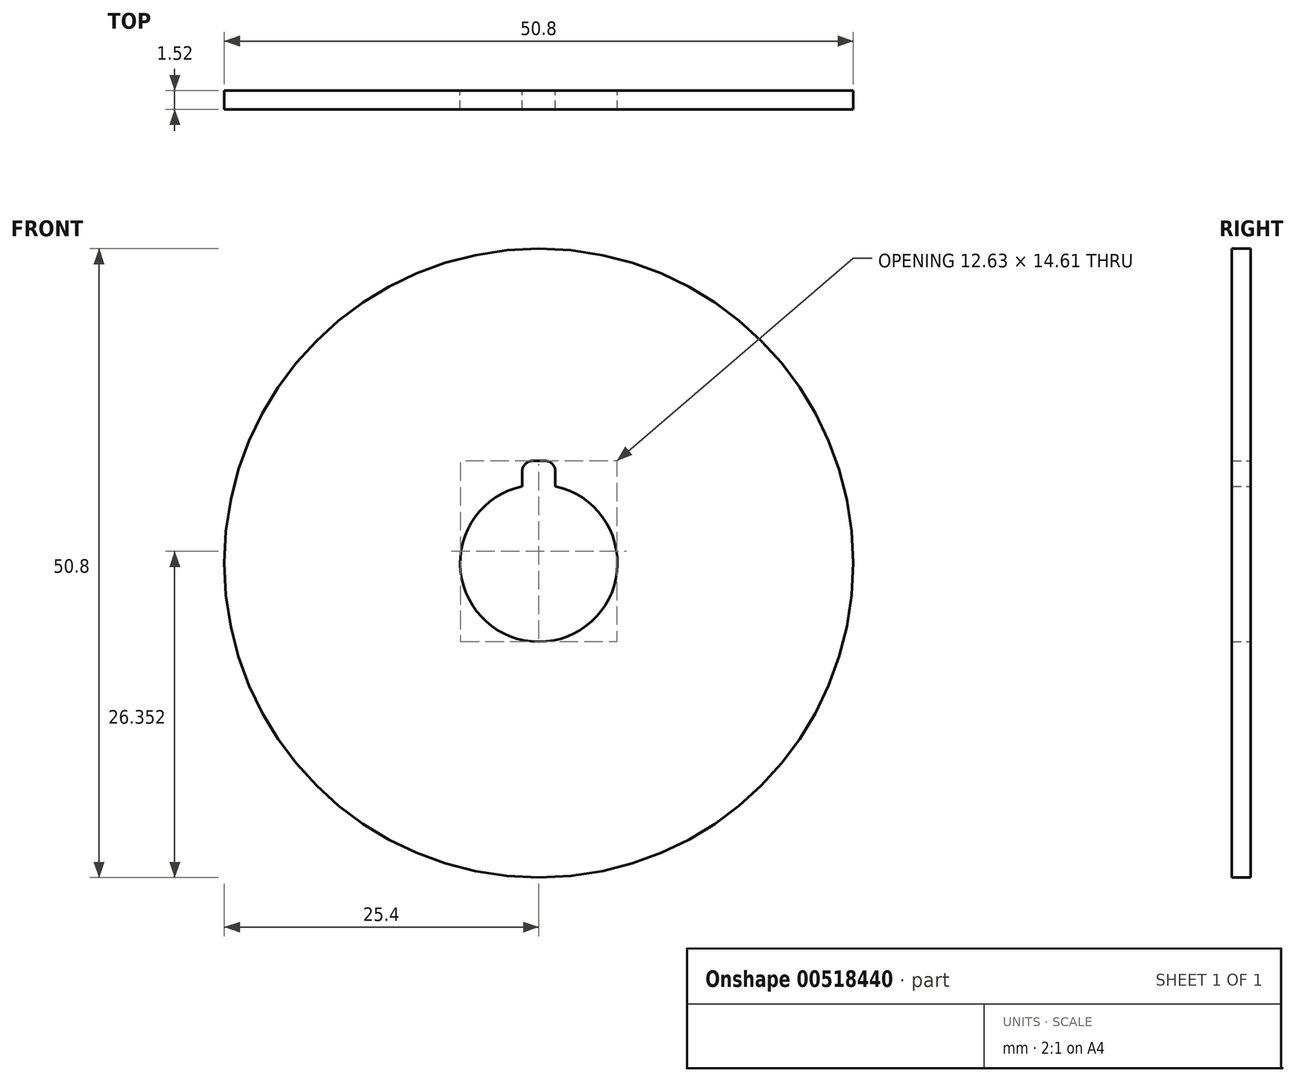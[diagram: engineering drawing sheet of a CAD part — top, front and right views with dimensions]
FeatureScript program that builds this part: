
annotation { "Feature Type Name" : "Feature", "Feature Type Description" : "" }
export const myFeature = defineFeature(function(context is Context, id is Id, definition is map)
    precondition{}
    {
        {
            var Q0;
            Q0=qCreatedBy(makeId("Front.planeOp"),FACE);
            var sketch = newSketch(context, id + "F0", { "sketchPlane" : qUnion([Q0])});
            skCircle(sketch, "E0", {"center": v(0, 0) * mm, "radius": 6.35 * mm});
            skCircle(sketch, "E1", {"center": v(0, 0) * mm, "radius": 25.4 * mm});
            skSolve(sketch);
        }
        {
            var Q0;
            Q0 = qSketchRegion(id + "F0", true);
            extrude(context, id + "F1", {"entities" : qUnion([Q0]), "depth" : 1.52 * mm, "offsetDistance" : 25.4 * mm});
        }
        {
            var Q0;
            Q0=qCreatedBy(makeId("Front.planeOp"),FACE);
            var sketch = newSketch(context, id + "F2", { "sketchPlane" : qUnion([Q0])});
            skLineSegment(sketch, "E2.bottom", {"start": v(-1.33, 8.25) * mm, "end": v(1.33, 8.25) * mm});
            skLineSegment(sketch, "E2.top", {"start": v(-1.33, 0) * mm, "end": v(1.33, 0) * mm});
            skLineSegment(sketch, "E2.left", {"start": v(-1.33, 8.25) * mm, "end": v(-1.33, 0) * mm});
            skLineSegment(sketch, "E2.right", {"start": v(1.33, 8.25) * mm, "end": v(1.33, 0) * mm});
            skPoint(sketch, "E3", {"position": v(0, -6.35) * mm});
            skSolve(sketch);
        }
        {
            var Q0;
            Q0=makeQuery(id+"F2.imprint","IMPRINT",FACE,{"disambiguationData":[TD([[makeQuery(id+"F2.imprint","IMPRINT",EDGE,{"derivedFrom":sQuery(id+"F2.wireOp",EDGE,"E2.bottom")}),-1.0]])]});
            var Q1;
            Q1=makeQuery(id+"F1.opExtrude","SWEPT_BODY",BODY,{"disambiguationData":[OSD([sQuery(id+"F0.wireOp",EDGE,"E0"),sQuery(id+"F0.wireOp",EDGE,"E1")])]});
            extrude(context, id + "F3", {"entities" : qUnion([Q0]), "operationType" : NewBodyOperationType.REMOVE, "endBound" : BoundingType.UP_TO_BODY, "depth" : 25.4 * mm, "endBoundEntityBody" : qUnion([Q1]), "offsetDistance" : 25.4 * mm});
        }
        {
            var Q0;
            Q0=makeQuery(id+"F3.boolean.opBoolean","COPY",EDGE,{"derivedFrom":makeQuery(id+"F3.opExtrude","SWEPT_EDGE",EDGE,{"disambiguationData":[OSD([sQuery(id+"F2.wireOp",EDGE,"E2.bottom"),sQuery(id+"F2.wireOp",EDGE,"E2.left")])]})});
            var Q1;
            Q1=makeQuery(id+"F3.boolean.opBoolean","COPY",EDGE,{"derivedFrom":makeQuery(id+"F3.opExtrude","SWEPT_EDGE",EDGE,{"disambiguationData":[OSD([sQuery(id+"F2.wireOp",EDGE,"E2.bottom"),sQuery(id+"F2.wireOp",EDGE,"E2.right")])]})});
            fillet(context, id + "F4", {"entities" : qUnion([Q0, Q1]), "radius" : 0.81 * mm, "tangentPropagation" : true, "allowEdgeOverflow" : false});
        }
    });
